# Revit family: PLASTIC CHANNEL BASE DN100 Slot Drain
name_source: partatom
category: Оборудование
units: mm (PartAtom-declared; Revit-internal decimal feet)

## family parameters
Общий = Да
Основа = Грань
При загрузке вырезать с полостями = Нет
Размер круглого соединителя = Использовать диаметр
Тип детали = Нормальный
Точка расчета площади = Нет

## types (38) — shared parameters
A01 = L-type H100 A15-C250 : 2017-1L-100 Galvanized Steel
A02 = L-type H100 A15-C250 : 2097-1L-100 Stainless steel
A03 = T-type H100 A15-C250 : 2017-1T-100 Galvanized Steel
A04 = T-type H100 A15-C250 : 2097-1T-100 Stainless steel
A05 = T-type H25 A15 : 2017-1T-25 Galvanized Steel
A06 = T-type H25 A15 : 2097-1T-25 Stainless steel
A07 = T-type H25 shifted A15 : 2017-1T-25-40 Galvanized Steel
A08 = T-type H25 shifted A15 : 2097-1T-25-40 Stainless steel
A09 = T-type H60-100 A15-C250 : 2097-1T-60-100 Stainless steel
A10 = L-type H25 A15 : 2087-L-25 Plastic
A11 = L-type H100 A15 : 2087-L-100 Plastic
ADSK_Dimension_Diameter = 110 мм
ADSK_Dimension_Lenght = 1000 мм
ADSK_Dimension_Width = 160 мм
ADSK_Load class = C250
ADSK_Manufacturer = Vodaland
ADSK_Material_Name = Plastic
ADSK_Unit = pcs
Cap1 = Plastic end cap Base DN100 : 630-1
Cap2 = Plastic end cap Base DN100 : 630-2
Cap3 = Plastic end cap Base DN100 : 630-3
Cap8010 = Plastic end cap Base DN100 : 630080
Cap8020 = Plastic end cap Base DN100 : 630120
Cap8050 = Plastic end cap Base DN100 : 630060
CapS01 = Endcap for Slot Drain Base DN100 : 6167-1L-100-L
CapS02 = Endcap for Slot Drain Base DN100 : 6167-1L-100-R
CapS03 = Endcap for Slot Drain Base DN100 : 6167-1T-25
CapS04 = Endcap for Slot Drain Base DN100 : 6167-1T-100
CapS05 = Endcap for Slot Drain Base DN100 : 6967-1L-100-L
CapS06 = Endcap for Slot Drain Base DN100 : 6967-1L-100-R
CapS07 = Endcap for Slot Drain Base DN100 : 6967-1T-25
CapS08 = Endcap for Slot Drain Base DN100 : 6967-1T-100
Co1 = Plastic end cap with outlet Base DN100 : 6308-1
Co2 = Plastic end cap with outlet Base DN100 : 6308-2
Co3 = Plastic end cap with outlet Base DN100 : 6308-3
Co4 = Plastic end cap with outlet Base DN100 : 6308-4
Co8050 = Plastic end cap with outlet Base DN100 : 6300608
Co805050 = Plastic end cap with outlet Base DN100 : 6300608-50
Connector = Plastic end cap with outlet Base DN100 : 6308-1
G01 = Slot Drain L-type H100 Base DN100 Channel A15-C250 : 2017-1L-100
G02 = Slot Drain L-type H100 Base DN100 Channel A15-C250 : 2097-1L-100
G03 = Slot Drain T-type H100 Base DN100 Channel A15-C250 : 2017-1T-100
G04 = Slot Drain T-type H100 Base DN100 Channel A15-C250 : 2097-1T-100
G05 = Slot Drain T-type H25 Base DN100 Channel A15 : 2017-1T-25
G06 = Slot Drain T-type H25 Base DN100 Channel A15 : 2097-1T-25
G07 = Slot Drain T-type H25 for Base DN100 Channel A15 : 2017-1T-25-40
G08 = Slot Drain T-type H25 for Base DN100 Channel A15 : 2097-1T-25-40
G09 = Slot Drain T-type H60-100 for Base DN100 Channel A15-C250 : 2097-1T-60-100
G10 = Slot drain L-type H25 for channel Base DN100 plastic A15 : 2087-L-25
G11 = Slot drain L-type H100 for channel Base DN100 plastic A15 : 2087-L-100
W1 = 160 мм
W2 = 156 мм
bias = Нет
no = No
Группа модели = Linear drainage
zero-valued in all types: Отметка по умолчанию

## per-type parameters (varying)
| type | ADSK_Dimension_Height | ADSK_Name | ADSK_Sealant | ADSK_Weight | CN | Cap_begin | Cap_end | H1 | H2 | R1 | R2 |
| 80060 | 60 мм | Plastic channel Base DN100 H60 | 10 | 1.2 | 8050 | Plastic end cap Base DN100 : 630060 | Plastic end cap Base DN100 : 630060 | 20 мм | 20 мм | 5 мм | 5 мм |
| 80080-1 | 80 мм | Plastic slope channel Base DN100 H80 1 | 11 | 1.4 | 80080 | Plastic end cap Base DN100 : 630060 | Plastic end cap Base DN100 : 630-1 | 40 мм | 40 мм | 5 мм | 25 мм |
| 80080 | 80 мм | Plastic channel Base DN100 H80 | 11 | 1.2 | 8010 | Plastic end cap Base DN100 : 630080 | Plastic end cap Base DN100 : 630080 | 40 мм | 40 мм | 25 мм | 25 мм |
| 80090-2 | 90 мм | Plastic slope channel Base DN100 H90 2 | 11 | 1.4 | 80090 | Plastic end cap Base DN100 : 630-1 | Plastic end cap Base DN100 : 630-1 | 50 мм | 50 мм | 25 мм | 25 мм |
| 80100-3 | 100 мм | Plastic slope channel Base DN100 H100 3 | 12 | 1.5 | 80100 | Plastic end cap Base DN100 : 630-1 | Plastic end cap Base DN100 : 630-2 | 60 мм | 60 мм | 25 мм | 49 мм |
| 80100 | 100 мм | Plastic channel Base DN100 H100 | 12 | 1.4 | 80100 | Plastic end cap Base DN100 : 630-1 | Plastic end cap Base DN100 : 630-2 | 60 мм | 60 мм | 49 мм | 49 мм |
| 80110-4 | 110 мм | Plastic slope channel Base DN100 H110 4 | 12 | 1.7 | 80110 | Plastic end cap Base DN100 : 630-2 | Plastic end cap Base DN100 : 630-2 | 70 мм | 70 мм | 49 мм | 49 мм |
| 80120-5 | 120 мм | Plastic slope channel Base DN100 H120 5 | 13 | 1.8 | 80120 | Plastic end cap Base DN100 : 630-2 | Plastic end cap Base DN100 : 630-2 | 80 мм | 80 мм | 49 мм | 49 мм |
| 80120 | 120 мм | Plastic channel Base DN100 H120 | 13 | 1.8 | 8020 | Plastic end cap Base DN100 : 630120 | Plastic end cap Base DN100 : 630120 | 80 мм | 80 мм | 49 мм | 49 мм |
| 80130-6 | 130 мм | Plastic slope channel Base DN100 H130 6 | 14 | 1.8 | 80130 | Plastic end cap Base DN100 : 630-2 | Plastic end cap Base DN100 : 630-2 | 90 мм | 90 мм | 49 мм | 49 мм |
| 80140-7 | 140 мм | Plastic slope channel Base DN100 H140 7 | 14 | 1.9 | 80140 | Plastic end cap Base DN100 : 630-2 | Plastic end cap Base DN100 : 630-2 | 100 мм | 100 мм | 49 мм | 49 мм |
| 80150-8 | 150 мм | Plastic slope channel Base DN100 H150 8 | 16 | 2 | 80150 | Plastic end cap Base DN100 : 630-2 | Plastic end cap Base DN100 : 630-2 | 110 мм | 110 мм | 49 мм | 49 мм |
| 80150 | 150 мм | Plastic channel Base DN100 H150 | 16 | 2.1 | 8000 | Plastic end cap Base DN100 : 630-2 | Plastic end cap Base DN100 : 630-2 | 110 мм | 110 мм | 49 мм | 49 мм |
| 80160-9 | 160 мм | Plastic slope channel Base DN100 H160 9 | 17 | 2.1 | 80160 | Plastic end cap Base DN100 : 630-2 | Plastic end cap Base DN100 : 630-3 | 120 мм | 120 мм | 49 мм | 49 мм |
| 80170-10 | 170 мм | Plastic slope channel Base DN100 H170 10 | 18 | 2.2 | 80170 | Plastic end cap Base DN100 : 630-3 | Plastic end cap Base DN100 : 630-3 | 130 мм | 130 мм | 49 мм | 49 мм |
| 80180-11 | 180 мм | Plastic slope channel Base DN100 H180 11 | 19 | 2.3 | 80180 | Plastic end cap Base DN100 : 630-3 | Plastic end cap Base DN100 : 630-3 | 140 мм | 140 мм | 49 мм | 49 мм |
| 80190-12 | 190 мм | Plastic slope channel Base DN100 H190 12 | 20 | 2.4 | 80190 | Plastic end cap Base DN100 : 630-3 | Plastic end cap Base DN100 : 630-3 | 150 мм | 150 мм | 49 мм | 49 мм |
| 80200-13 | 200 мм | Plastic slope channel Base DN100 H200 13 | 21 | 2.5 | 80200 | Plastic end cap Base DN100 : 630-3 | Plastic end cap Base DN100 : 630-3 | 160 мм | 160 мм | 49 мм | 49 мм |
| 80200 | 200 мм | Plastic channel Base DN100 H200 | 21 | 2.5 | 80200 | Plastic end cap Base DN100 : 630-3 | Plastic end cap Base DN100 : 630-3 | 160 мм | 160 мм | 49 мм | 49 мм |
| 80067 | 60 мм | Plastic channel Base DN100 H60 reinforced | 10 | 1.2 | 8050 | Plastic end cap Base DN100 : 630060 | Plastic end cap Base DN100 : 630060 | 20 мм | 20 мм | 5 мм | 5 мм |
| 80087-1 | 80 мм | Plastic slope channel Base DN100 H80 1 reinforced | 11 | 1.4 | 80080 | Plastic end cap Base DN100 : 630060 | Plastic end cap Base DN100 : 630-1 | 40 мм | 40 мм | 5 мм | 25 мм |
| 80087 | 80 мм | Plastic channel Base DN100 H80 reinforced | 11 | 1.2 | 8010 | Plastic end cap Base DN100 : 630080 | Plastic end cap Base DN100 : 630080 | 40 мм | 40 мм | 25 мм | 25 мм |
| 80097-2 | 90 мм | Plastic slope channel Base DN100 H90 2 reinforced | 11 | 1.4 | 80090 | Plastic end cap Base DN100 : 630-1 | Plastic end cap Base DN100 : 630-1 | 50 мм | 50 мм | 25 мм | 25 мм |
| 80107-3 | 100 мм | Plastic slope channel Base DN100 H100 3 reinforced | 12 | 1.5 | 80100 | Plastic end cap Base DN100 : 630-1 | Plastic end cap Base DN100 : 630-2 | 60 мм | 60 мм | 25 мм | 49 мм |
| 80107 | 100 мм | Plastic channel Base DN100 H100 reinforced | 12 | 1.4 | 80100 | Plastic end cap Base DN100 : 630-1 | Plastic end cap Base DN100 : 630-2 | 60 мм | 60 мм | 49 мм | 49 мм |
| 80117-4 | 110 мм | Plastic slope channel Base DN100 H110 4 reinforced | 12 | 1.7 | 80110 | Plastic end cap Base DN100 : 630-2 | Plastic end cap Base DN100 : 630-2 | 70 мм | 70 мм | 49 мм | 49 мм |
| 80127-5 | 120 мм | Plastic slope channel Base DN100 H120 5 reinforced | 13 | 1.8 | 80120 | Plastic end cap Base DN100 : 630-2 | Plastic end cap Base DN100 : 630-2 | 80 мм | 80 мм | 49 мм | 49 мм |
| 80127 | 120 мм | Plastic channel Base DN100 H120 reinforced | 13 | 1.8 | 8020 | Plastic end cap Base DN100 : 630120 | Plastic end cap Base DN100 : 630120 | 80 мм | 80 мм | 49 мм | 49 мм |
| 80137-6 | 130 мм | Plastic slope channel Base DN100 H130 6 reinforced | 14 | 1.8 | 80130 | Plastic end cap Base DN100 : 630-2 | Plastic end cap Base DN100 : 630-2 | 90 мм | 90 мм | 49 мм | 49 мм |
| 80147-7 | 140 мм | Plastic slope channel Base DN100 H140 7 reinforced | 14 | 1.9 | 80140 | Plastic end cap Base DN100 : 630-2 | Plastic end cap Base DN100 : 630-2 | 100 мм | 100 мм | 49 мм | 49 мм |
| 80157-8 | 150 мм | Plastic slope channel Base DN100 H150 8 reinforced | 16 | 2 | 80150 | Plastic end cap Base DN100 : 630-2 | Plastic end cap Base DN100 : 630-2 | 110 мм | 110 мм | 49 мм | 49 мм |
| 80157 | 150 мм | Plastic channel Base DN100 H150 reinforced | 16 | 2.1 | 8000 | Plastic end cap Base DN100 : 630-2 | Plastic end cap Base DN100 : 630-2 | 110 мм | 110 мм | 49 мм | 49 мм |
| 80167-9 | 160 мм | Plastic slope channel Base DN100 H160 9 reinforced | 17 | 2.1 | 80160 | Plastic end cap Base DN100 : 630-2 | Plastic end cap Base DN100 : 630-3 | 120 мм | 120 мм | 49 мм | 49 мм |
| 80177-10 | 170 мм | Plastic slope channel Base DN100 H170 10 reinforced | 18 | 2.2 | 80170 | Plastic end cap Base DN100 : 630-3 | Plastic end cap Base DN100 : 630-3 | 130 мм | 130 мм | 49 мм | 49 мм |
| 80187-11 | 180 мм | Plastic slope channel Base DN100 H180 11 reinforced | 19 | 2.3 | 80180 | Plastic end cap Base DN100 : 630-3 | Plastic end cap Base DN100 : 630-3 | 140 мм | 140 мм | 49 мм | 49 мм |
| 80197-12 | 190 мм | Plastic slope channel Base DN100 H190 12 reinforced | 20 | 2.4 | 80190 | Plastic end cap Base DN100 : 630-3 | Plastic end cap Base DN100 : 630-3 | 150 мм | 150 мм | 49 мм | 49 мм |
| 80207-13 | 200 мм | Plastic slope channel Base DN100 H200 13 reinforced | 21 | 2.5 | 80200 | Plastic end cap Base DN100 : 630-3 | Plastic end cap Base DN100 : 630-3 | 160 мм | 160 мм | 49 мм | 49 мм |
| 80207 | 200 мм | Plastic channel Base DN100 H200 reinforced | 21 | 2.5 | 80200 | Plastic end cap Base DN100 : 630-3 | Plastic end cap Base DN100 : 630-3 | 160 мм | 160 мм | 49 мм | 49 мм |

note: column(s) folded — value = type name in every type: ADSK_Product code

## geometry (parser evidence)
native form markers: Blend x8
no freeform markers — native parametric forms only
